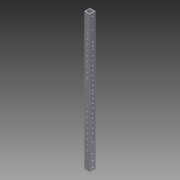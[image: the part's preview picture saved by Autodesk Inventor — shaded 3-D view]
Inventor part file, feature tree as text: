
AUTODESK INVENTOR PART (.ipt)
format: ipt  version: 2013 (Build 170138000, 138)  size: 269,824 bytes
history: native  units: in
note: dims shown in document units (in); Inventor stores cm internally (conversion verified against a paired STEP export)
features: extrude x4, sketch x4
ambient origin geometry x8: Origin, YZ Plane, XZ Plane, XY Plane, X Axis, Y Axis, Z Axis, Center Point
bodies: Solid1 (feature_tree)
feature tree (8):
  extrude  "Extrusion1"  Depth=1.0in
  extrude  "Extrusion2"  Depth=24.0in TaperAngle=0.0deg
  extrude  "Extrusion3"  Depth=0.26in
  extrude  "Extrusion4"  Depth=11.0236in
  sketch  "Sketch1"  dims[d0=1.0in d1=1.0in]
  sketch  "Sketch2"  dims[d2=0.125in d3=24.0in d4=0.0in]
  sketch  "Sketch3"  dims[d5=0.55in d6=0.26in]
  sketch  "Sketch4"  dims[d7=24.0in d8=11.0236in d10=0.8481in d11=0.3937in d13=1.0in d15=1.0in d16=0.0in d17=1.75in d18=2.0in d19=1.75in d20=1.75in d21=0.26in d22=0.26in d23=0.26in d24=0.26in d25=0.26in d26=0.26in d27=0.26in d28=0.26in d29=1.0in d30=0.0in d31=2.0in d32=0.26in d33=0.26in d40=0.5in d41=0.26in d42=0.5in d43=0.26in d46=0.75in d47=0.75in d48=0.26in d49=0.26in d50=1.0in d51=0.0in d52=0.26in d53=5.5in d64=1.0in d65=0.26in d66=0.55in d67=24.0in d68=11.0236in d70=0.8481in d71=0.3937in d73=1.0in d76=0.375in d77=0.375in d85=0.5in d86=2.7559in d88=0.75in d89=0.3937in d91=1.0in d93=2.3622in d95=0.75in d96=0.3937in d98=1.0in d100=0.75in d101=0.75in]
